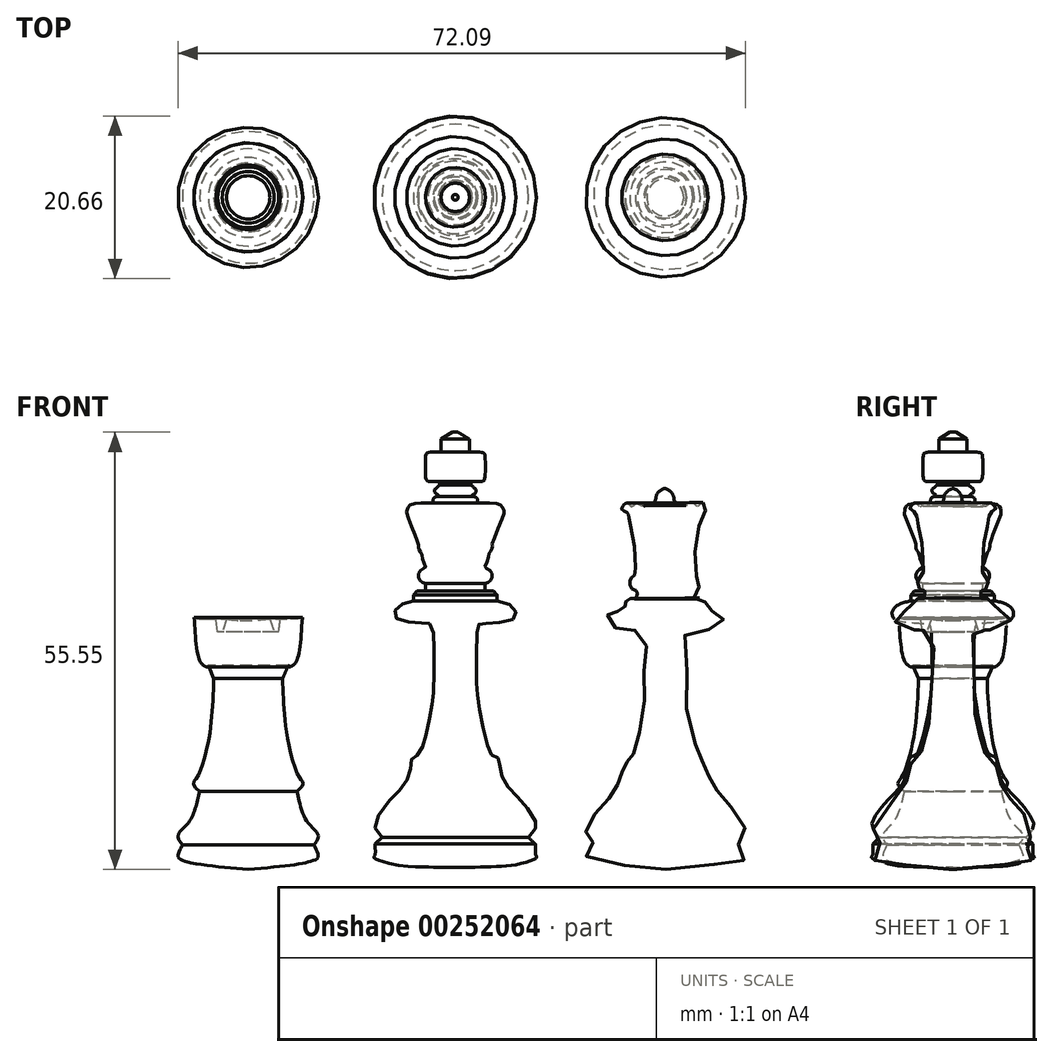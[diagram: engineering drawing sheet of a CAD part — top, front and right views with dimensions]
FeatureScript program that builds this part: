
annotation { "Feature Type Name" : "Feature", "Feature Type Description" : "" }
export const myFeature = defineFeature(function(context is Context, id is Id, definition is map)
    precondition{}
    {
        {
            var Q0;
            Q0=qCreatedBy(makeId("Front.planeOp"),FACE);
            var sketch = newSketch(context, id + "F0", { "sketchPlane" : qUnion([Q0])});
            skFitSpline(sketch, "E0", {"points": [v(0, 0.27) * mm, v(1.06, 0.25) * mm, v(4.53, 0.34) * mm, v(8, 0.67) * mm, v(10.26, 1.42) * mm, v(10.33, 1.53) * mm, v(10.27, 1.7) * mm, v(10.2, 1.82) * mm, v(10.18, 3.22) * mm], "startDerivative": vector(7.48, -0.23) * mm, "endDerivative": vector(0.52, 13.25) * mm});
            skLineSegment(sketch, "E1", {"start": v(9.3, 4.08) * mm, "end": v(10.18, 3.22) * mm});
            skFitSpline(sketch, "E2", {"points": [v(9.3, 4.08) * mm, v(10.06, 5.01) * mm, v(10.29, 5.64) * mm, v(10.23, 6.05) * mm, v(9.13, 7.83) * mm, v(7.65, 9.45) * mm, v(6.52, 10.7) * mm, v(5.92, 11.87) * mm, v(5.61, 13.35) * mm, v(5.58, 13.9) * mm, v(5.47, 14.1) * mm, v(5.12, 14.42) * mm, v(4.66, 14.52) * mm, v(4.43, 14.8) * mm, v(3.77, 16.99) * mm, v(3.1, 20.07) * mm, v(2.8, 22.17) * mm, v(2.72, 22.9) * mm, v(2.7, 29.12) * mm, v(2.84, 30.85) * mm, v(2.99, 31.14) * mm, v(3.24, 31.25) * mm, v(3.98, 31.28) * mm, v(5.69, 31.4) * mm, v(7.32, 31.77) * mm, v(7.7, 32.33) * mm, v(7.6, 33) * mm, v(6.84, 33.66) * mm, v(5.3, 34.12) * mm], "startDerivative": vector(24.46, 25.84) * mm, "endDerivative": vector(-39.62, 8.67) * mm});
            skFitSpline(sketch, "E3", {"points": [v(5.3, 34.12) * mm, v(5.3, 34.9) * mm], "startDerivative": vector(0, 0.77) * mm, "endDerivative": vector(0, 0.77) * mm});
            skFitSpline(sketch, "E4", {"points": [v(5.3, 34.9) * mm, v(4.86, 35.39) * mm], "startDerivative": vector(-0.45, 0.49) * mm, "endDerivative": vector(-0.45, 0.49) * mm});
            skFitSpline(sketch, "E5", {"points": [v(4.86, 35.39) * mm, v(3.79, 35.39) * mm], "startDerivative": vector(-1.07, 0) * mm, "endDerivative": vector(-1.07, 0) * mm});
            skFitSpline(sketch, "E6", {"points": [v(3.79, 35.39) * mm, v(3.79, 36.3) * mm], "startDerivative": vector(0, 0.92) * mm, "endDerivative": vector(0, 0.92) * mm});
            skFitSpline(sketch, "E7", {"points": [v(3.79, 36.3) * mm, v(4.2, 36.5) * mm, v(4.59, 36.86) * mm, v(4.64, 37.59) * mm, v(4.24, 38.13) * mm, v(3.79, 38.4) * mm, v(4.13, 39.35) * mm, v(4.3, 40.2) * mm, v(4.5, 40.45) * mm, v(4.7, 40.9) * mm, v(4.7, 41.19) * mm, v(4.7, 41.38) * mm, v(6.09, 45) * mm, v(6.17, 45.55) * mm, v(5.98, 46.05) * mm, v(5.52, 46.43) * mm, v(2.82, 46.5) * mm], "startDerivative": vector(8.47, 3.37) * mm, "endDerivative": vector(-27.55, -1.35) * mm});
            skFitSpline(sketch, "E8", {"points": [v(2.82, 46.5) * mm, v(2.82, 47) * mm, v(2.68, 47.25) * mm, v(2.4, 47.36) * mm, v(2.15, 47.38) * mm], "startDerivative": vector(0.12, 1.74) * mm, "endDerivative": vector(-1.06, 0.08) * mm});
            skFitSpline(sketch, "E9", {"points": [v(2.15, 47.38) * mm, v(2.15, 47.57) * mm, v(2.4, 47.73) * mm, v(2.6, 47.91) * mm, v(2.65, 48.18) * mm, v(2.5, 48.4) * mm, v(2.15, 48.7) * mm, v(1.99, 48.84) * mm], "startDerivative": vector(-0.4, 1.7) * mm, "endDerivative": vector(-1.12, 1.04) * mm});
            skFitSpline(sketch, "E10", {"points": [v(1.99, 48.84) * mm, v(1.99, 49.32) * mm], "startDerivative": vector(0, 0.48) * mm, "endDerivative": vector(0, 0.48) * mm});
            skFitSpline(sketch, "E11", {"points": [v(1.99, 49.32) * mm, v(3.46, 49.32) * mm], "startDerivative": vector(1.47, 0) * mm, "endDerivative": vector(1.47, 0) * mm});
            skFitSpline(sketch, "E12", {"points": [v(3.46, 49.32) * mm, v(3.62, 49.4) * mm, v(3.78, 50.01) * mm, v(3.75, 52.65) * mm, v(3.66, 52.85) * mm, v(3.46, 52.96) * mm, v(1.8, 53.04) * mm], "startDerivative": vector(2.03, 0.76) * mm, "endDerivative": vector(-8.09, 0.02) * mm});
            skFitSpline(sketch, "E13", {"points": [v(1.8, 54.65) * mm, v(1.8, 53.04) * mm], "startDerivative": vector(0, -1.61) * mm, "endDerivative": vector(0, -1.61) * mm});
            skFitSpline(sketch, "E14", {"points": [v(1.8, 54.65) * mm, v(0.37, 55.55) * mm], "startDerivative": vector(-1.43, 0.9) * mm, "endDerivative": vector(-1.43, 0.9) * mm});
            skFitSpline(sketch, "E15", {"points": [v(0.37, 55.55) * mm, v(0, 55.55) * mm], "startDerivative": vector(-0.37, 0) * mm, "endDerivative": vector(-0.37, 0) * mm});
            skLineSegment(sketch, "E16", {"start": v(0, 55.55) * mm, "end": v(0, 0) * mm});
            skFitSpline(sketch, "E17", {"points": [v(26.75, 0) * mm, v(34.47, 0.77) * mm, v(36.73, 1.24) * mm, v(36.73, 2.1) * mm, v(35.95, 3.26) * mm, v(36.73, 4.35) * mm, v(36.73, 5.51) * mm, v(35.4, 7.53) * mm, v(33.85, 9.17) * mm, v(33.15, 10.18) * mm, v(32.68, 11.03) * mm, v(32.22, 11.89) * mm, v(32.22, 13.13) * mm, v(31.2, 13.9) * mm, v(30.97, 14.14) * mm, v(30.5, 15.77) * mm, v(29.38, 20.5) * mm, v(29.38, 25.71) * mm, v(29.28, 29.94) * mm, v(31.54, 30.44) * mm, v(33.42, 30.93) * mm, v(34, 31.62) * mm, v(34, 32.3) * mm, v(33.32, 32.7) * mm, v(31.94, 33.1) * mm, v(31.74, 33.49) * mm, v(31.75, 33.88) * mm, v(31.43, 34.26) * mm, v(31.02, 34.47) * mm, v(30.35, 34.46) * mm, v(30.25, 35.4) * mm, v(30.6, 35.5) * mm, v(31.08, 36.12) * mm, v(31.08, 36.76) * mm, v(30.72, 37.27) * mm, v(30.54, 37.38) * mm, v(30.43, 39.65) * mm, v(30.68, 42.18) * mm, v(31.15, 44.52) * mm, v(31.37, 45.35) * mm, v(32.02, 45.71) * mm, v(32.09, 45.9) * mm, v(31.8, 46.33) * mm, v(31.37, 46.58) * mm, v(30.75, 46.11) * mm, v(30.28, 46.5) * mm, v(29.63, 46.3) * mm, v(28.84, 46.3) * mm, v(28.15, 46.58) * mm, v(27.83, 46.8) * mm, v(27.72, 47.37) * mm, v(27.29, 48.06) * mm, v(26.6, 48.42) * mm], "startDerivative": vector(172.13, 18.64) * mm, "endDerivative": vector(-46.17, 18.18) * mm});
            skLineSegment(sketch, "E18", {"start": v(26.6, 48.42) * mm, "end": v(26.75, 0) * mm});
            skLineSegment(sketch, "E19", {"start": v(-26.3, 0) * mm, "end": v(-26.3, 45.62) * mm});
            skLineSegment(sketch, "E20", {"start": v(-26.3, 45.62) * mm, "end": v(-26.3, -6.06) * mm});
            skFitSpline(sketch, "E21", {"points": [v(-26.3, 0) * mm, v(-20.07, 0.66) * mm, v(-18.27, 1.06) * mm, v(-17.48, 1.45) * mm, v(-17.48, 2.09) * mm, v(-17.94, 3.15) * mm], "startDerivative": vector(19.12, 1.7) * mm, "endDerivative": vector(-3.37, 6.8) * mm});
            skFitSpline(sketch, "E22", {"points": [v(-17.94, 3.15) * mm, v(-17.48, 3.81) * mm, v(-17.48, 4.54) * mm, v(-18.47, 5.64) * mm, v(-19.34, 7.07) * mm, v(-19.87, 8.76) * mm, v(-20.13, 9.93) * mm], "startDerivative": vector(4.05, 4.73) * mm, "endDerivative": vector(-1.45, 6.74) * mm});
            skFitSpline(sketch, "E23", {"points": [v(-20.13, 9.93) * mm, v(-19.4, 10.72) * mm, v(-19.44, 11.22) * mm, v(-19.83, 11.72) * mm, v(-21.13, 15.7) * mm, v(-21.66, 19.43) * mm, v(-21.86, 22.05) * mm, v(-21.92, 24.24) * mm], "startDerivative": vector(8.72, 7.36) * mm, "endDerivative": vector(-0.21, 14) * mm});
            skFitSpline(sketch, "E24", {"points": [v(-21.92, 24.24) * mm, v(-21.25, 25.9) * mm], "startDerivative": vector(0.67, 1.66) * mm, "endDerivative": vector(0.67, 1.66) * mm});
            skFitSpline(sketch, "E25", {"points": [v(-21.25, 25.9) * mm, v(-20.96, 25.75) * mm, v(-20.67, 25.9) * mm, v(-20.13, 26.52) * mm, v(-19.44, 32) * mm], "startDerivative": vector(2.25, -1.7) * mm, "endDerivative": vector(0.78, 12.82) * mm});
            skFitSpline(sketch, "E26", {"points": [v(-19.44, 32) * mm, v(-20.13, 31.84) * mm, v(-20.96, 31.83) * mm, v(-22.22, 31.84) * mm], "startDerivative": vector(-2.34, -0.64) * mm, "endDerivative": vector(-3.38, 0.02) * mm});
            skFitSpline(sketch, "E27", {"points": [v(-22.22, 31.84) * mm, v(-22.44, 30.18) * mm], "startDerivative": vector(-0.22, -1.66) * mm, "endDerivative": vector(-0.22, -1.66) * mm});
            skFitSpline(sketch, "E28", {"points": [v(-22.44, 30.18) * mm, v(-23.01, 30.18) * mm], "startDerivative": vector(-0.57, 0) * mm, "endDerivative": vector(-0.57, 0) * mm});
            skFitSpline(sketch, "E29", {"points": [v(-23.01, 30.18) * mm, v(-23.56, 31.84) * mm], "startDerivative": vector(-0.54, 1.66) * mm, "endDerivative": vector(-0.54, 1.66) * mm});
            skFitSpline(sketch, "E30", {"points": [v(-23.56, 31.84) * mm, v(-24.2, 31.72) * mm, v(-25.4, 31.65) * mm, v(-26.3, 31.72) * mm], "startDerivative": vector(-2.05, -0.48) * mm, "endDerivative": vector(-2.55, 0.29) * mm});
            skSolve(sketch);
        }
        {
            var Q0;
            {var subQ0=sQuery(id+"F0.wireOp",EDGE,"E0");Q0=makeQuery(id+"F0.imprint","IMPRINT",FACE,{"disambiguationData":[TD([[makeQuery(id+"F0.imprint","IMPRINT",EDGE,{"derivedFrom":subQ0}),1.0]])]});}
            var Q1;
            Q1=sQuery(id+"F0.wireOp",EDGE,"E16");
            revolve(context, id + "F1", {"surfaceOperationType" : NewSurfaceOperationType.NEW, "entities" : qUnion([Q0]), "axis" : qUnion([Q1]), "revolveType" : RevolveType.FULL});
        }
        {
            var Q0;
            Q0=makeQuery(id+"F0.imprint","IMPRINT",FACE,{"disambiguationData":[TD([[makeQuery(id+"F0.imprint","IMPRINT",EDGE,{"derivedFrom":sQuery(id+"F0.wireOp",EDGE,"E17")}),1.0]])]});
            var Q1;
            Q1=sQuery(id+"F0.wireOp",EDGE,"E18");
            revolve(context, id + "F2", {"surfaceOperationType" : NewSurfaceOperationType.NEW, "entities" : qUnion([Q0]), "axis" : qUnion([Q1]), "revolveType" : RevolveType.FULL, "oppositeDirection" : true});
        }
        {
            var Q0;
            {var subQ0=sQuery(id+"F0.wireOp",EDGE,"E21");Q0=makeQuery(id+"F0.imprint","IMPRINT",FACE,{"disambiguationData":[TD([[makeQuery(id+"F0.imprint","IMPRINT",EDGE,{"derivedFrom":subQ0}),1.0]])]});}
            var Q1;
            Q1=sQuery(id+"F0.wireOp",EDGE,"E20");
            revolve(context, id + "F3", {"surfaceOperationType" : NewSurfaceOperationType.NEW, "entities" : qUnion([Q0]), "axis" : qUnion([Q1]), "revolveType" : RevolveType.FULL});
        }
    });
